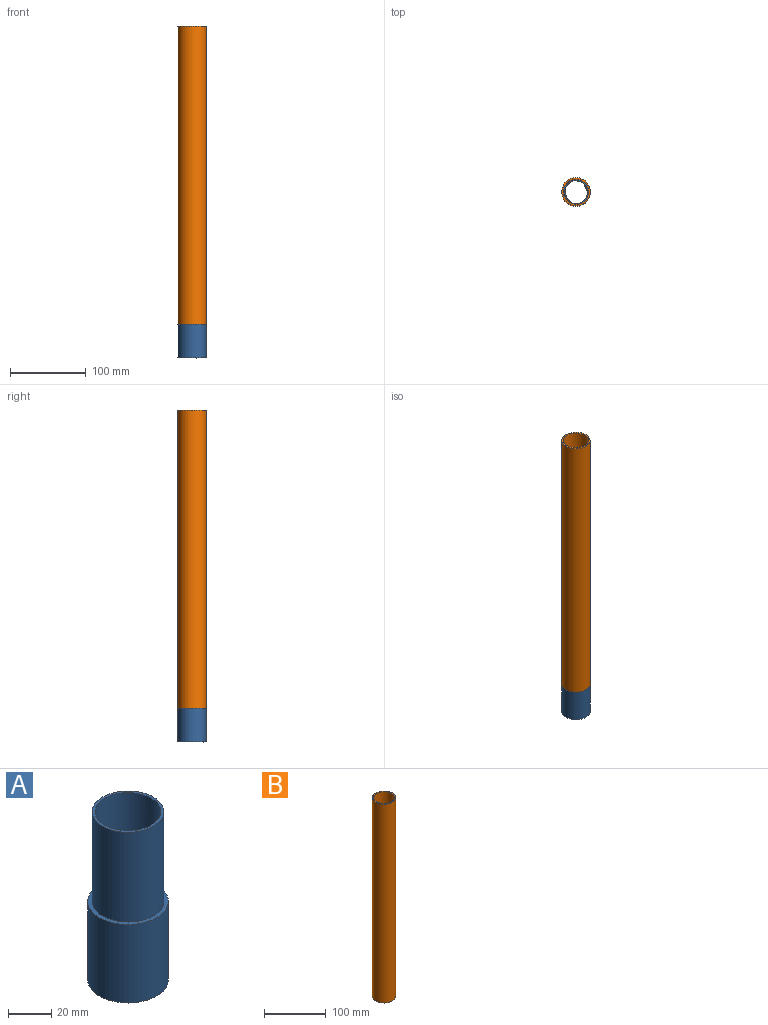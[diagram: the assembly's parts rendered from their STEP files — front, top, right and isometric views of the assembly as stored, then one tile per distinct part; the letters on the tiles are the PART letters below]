
ASSEMBLY  parts=2 mates=1
PART A: 40 faces, bbox 37.9x37.9x96.4 mm
  f0: cylinder r=15.24mm len=30.48mm, axis (0,0,-1), area 0mm2, adj f1
  f1: cylinder r=15.24mm len=30.48mm, axis (0,0,-1), area 0mm2, adj f0,f2,f39
  f2: bspline ~35.66x35.14mm, area 534.9mm2, adj f1,f3,f4,f5,f6,f7,f8,f9
  f3: cylinder r=15.24mm len=30.48mm, axis (0,0,-1), area 0mm2, adj f2,f39
  f4: cylinder r=15.24mm len=30.48mm, axis (0,0,-1), area 0mm2, adj f2,f5,f39
  f5: cylinder r=15.24mm len=30.48mm, axis (0,0,-1), area 0mm2, adj f2,f4,f6,f39
  f6: cylinder r=15.24mm len=30.48mm, axis (0,0,-1), area 0.1mm2, adj f2,f5,f7,f39
  f7: cylinder r=15.24mm len=30.48mm, axis (0,0,-1), area -0.1mm2, adj f2,f6,f8,f39
  f8: cylinder r=15.24mm len=30.48mm, axis (0,0,-1), area 0.1mm2, adj f2,f7,f9,f39
  f9: cylinder r=15.24mm len=30.48mm, axis (0,0,-1), area 0mm2, adj f2,f8,f10,f39
  f10: cylinder r=15.24mm len=30.48mm, axis (0,0,-1), area 0mm2, adj f2,f9,f11,f39
  f11: cylinder r=15.24mm len=30.48mm, axis (0,0,-1), area 0mm2, adj f10
  f12: cylinder r=15.24mm len=30.48mm, axis (0,0,-1), area 0mm2, adj f2,f39
  f13: cylinder r=15.24mm len=30.48mm, axis (0,0,-1), area 0mm2, adj f2,f14,f39
  f14: cylinder r=15.24mm len=30.48mm, axis (0,0,-1), area 0mm2, adj f2,f13,f15,f39
  f15: cylinder r=15.24mm len=30.48mm, axis (0,0,-1), area 0mm2, adj f2,f14,f16,f39
  f16: cylinder r=15.24mm len=30.48mm, axis (0,0,-1), area 0mm2, adj f2,f15,f17,f39
  f17: cylinder r=15.24mm len=30.48mm, axis (0,0,-1), area 0mm2, adj f2,f16,f18,f39
  f18: cylinder r=15.24mm len=30.48mm, axis (0,0,-1), area 0mm2, adj f2,f17,f19,f39
  f19: cylinder r=15.24mm len=30.48mm, axis (0,0,-1), area 0mm2, adj f2,f18,f20,f39
  f20: cylinder r=15.24mm len=30.48mm, axis (0,0,-1), area 0.1mm2, adj f2,f19,f21,f39
  f21: cylinder r=15.24mm len=30.48mm, axis (0,0,-1), area -0.1mm2, adj f2,f20,f22,f39
  f22: cylinder r=15.24mm len=30.48mm, axis (0,0,-1), area 0.1mm2, adj f2,f21,f23,f39
  f23: cylinder r=15.24mm len=30.48mm, axis (0,0,-1), area 0mm2, adj f2,f22,f24,f39
  f24: cylinder r=15.24mm len=30.48mm, axis (0,0,-1), area 0mm2, adj f2,f23,f25,f39
  f25: cylinder r=15.24mm len=30.48mm, axis (0,0,-1), area 0mm2, adj f24
  f26: cylinder r=15.24mm len=30.48mm, axis (0,0,-1), area 0mm2, adj f2,f39
  f27: plane 37.88x37.88mm, normal (0,0,-1), area 316.2mm2, adj f2,f28,f33,f34,f35,f36,f37,f39
  f28: cylinder r=18.67mm len=44.45mm, axis (0,0,-1), area 5214mm2, adj f27,f29
  f29: plane 37.34x37.34mm, normal (0,0,1), area 228mm2, adj f28,f30
  f30: cylinder r=16.61mm len=50.8mm, axis (0,0,-1), area 5302.2mm2, adj f29,f31
  f31: plane 33.22x33.22mm, normal (0,0,1), area 137.2mm2, adj f30,f32
  f32: cylinder r=15.24mm len=60.33mm, axis (0,0,-1), area 5715.7mm2, adj f31,f38,f39
  f33: bspline ~37.25x35.96mm, area 2186mm2, adj f27,f34,f37,f38
  f34: cylinder r=16.13mm len=35.64mm, axis (0,0,1), area 600.8mm2, adj f27,f33,f35,f38
  f35: bspline ~37.25x36.59mm, area 2223.7mm2, adj f27,f34,f36,f38
  f36: cylinder r=15.44mm len=36.2mm, axis (0,0,1), area 261.9mm2, adj f27,f35,f38,f39
  f37: cylinder r=15.44mm len=35.08mm, axis (0,0,1), area 1073.1mm2, adj f2,f27,f33,f38
  f38: plane 1.27x0.89mm, normal (0,-1,0), area 0.6mm2, adj f2,f32,f33,f34,f35,f36,f37,f39
  f39: bspline ~36.2x35.66mm, area 557.2mm2, adj f1,f2,f3,f4,f5,f6,f7,f8
PART B: 4 faces, bbox 37.3x37.3x392.8 mm
  f0: cylinder r=16.64mm len=392.81mm, axis (0,0,-1), area 41061.9mm2, adj f2,f3
  f1: cylinder r=18.67mm len=392.81mm, axis (0,0,-1), area 46077mm2, adj f2,f3
  f2: plane 37.34x37.34mm, normal (0,0,1), area 225.4mm2, adj f0,f1
  f3: plane 37.34x37.34mm, normal (0,0,-1), area 225.4mm2, adj f0,f1
PLACE A t=(-88.41,39.26,30.99)mm
PLACE B t=(-88.41,39.26,75.44)mm
MATE fastened A.f30 <-> B.f1  axis (0,0,1) through (-88.41,39.26,75.44)mm
